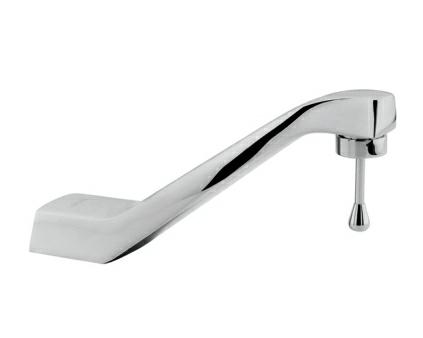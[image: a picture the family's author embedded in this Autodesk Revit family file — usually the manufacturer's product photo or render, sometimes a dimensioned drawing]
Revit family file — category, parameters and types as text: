
# Revit family: TV105-2_RFA
name_source: partatom
category: Aparatos sanitarios
units: mm (PartAtom-declared; Revit-internal decimal feet)

## family parameters
Compartido = Sí
Corte con vacíos al cargar = No
Cota de conector redondo = Diámetro de uso
Número OmniClass = 23.45.00.00
Punto de cálculo de habitación = Sí
Se basa en plano de trabajo = Sí
Siempre vertical = Sí
Tipo de pieza = Normal
Título OmniClass = Sanitary, Laundry, and Cleaning Equipment

## types (1)
- TV-105
    Accessories = Economizador para autoajuste de flujo y palanca con recubrimiento antibacterial
    Chrome = Brass Chromed
    Comentarios de tipo = Llave Economizadora
    Compliance = NMX-C-415-ONNCCE-1999
    Connection = ½" - 14 NPSM
    Descripción = Llave Economizadora con Seguro Antirrobo
    Elevación por Defecto = 1"
    Elevación por defecto = 48"
    Fabricante = HELVEX S.A. DE C.V.
    Imagen de tipo = TV-105.jpg
    Max. Water Flow = 1.2 gal/min
    Max. Working Pressure = 85.3 psi
    Min. Working Pressure = 3.5 psi
    Modelo = TV-105
    Operation = Cierre Automático y Perilla multidireccional
    Total Height = 4"
    Total Length = 6"
    Total Width = 2"
    URL = http://www.helvex.com.mx
    Warranty = El producto HELVEX está garantizado como libre de defectos en materiales y procesos de fabricación. El producto HELVEX está garantizado, en lo que se refiere a los acabados; por un periodo de 10 años en los acabados cromo y duravex, y por 2 años en cabados diferentes al cromo, a partir de la fecha de compra indicada en la factura.

## geometry (parser evidence)
native form markers: Sweep x3
no freeform markers — native parametric forms only
